# Revit family: 2061270 Sylvania Lighting Fixture DOMINO 10xLED 940 OPAL AY TRIM BLACK
name_source: partatom
category: Lighting Fixtures
revit_build: Autodesk Revit 2018 (Build: 20170223_1515(x64)
units: mm (PartAtom-declared; Revit-internal decimal feet)

## family parameters
Cut with Voids When Loaded = No
Host = Face
Light Source = Yes
OmniClass Number = 23.80.70.00
OmniClass Title = Lighting
Part Type = Normal
Room Calculation Point = No
Round Connector Dimension = Use Diameter
Shared = No

## types (1)
- 2061270 DOMINO 10XLED 940 OPAL ASYM TR BLK
    Apparent Load = 23 VA
    Assembly Code = D5020200
    AssetType = Fixed
    Body Length = 270 mm
    Body Width = 40 mm
    ClassificationName = Uniclass2015
    ClassificationValue = EF_70_80
    Color Filter = 16777215
    Cost = 0 $
    Default Elevation = 1219 mm
    Description = Modular LED recessed linear spotlight, ideal for retail and hospitality applications. Die-cast aluminium body, passive cooling. Two levels of reflector installation, low glaring. 10x LED source, asymmetric beam angle , optics: PMMA lens and polycarbonate reflector combination, opaline diffuser. Light color temperature: 4000K neutral white, total system power: 23W , total fixture lumen output: 1475lm, efficacy: 65 lm/W, Ra90 typical, LED chromacity: 3 step MacAdam ellipse (SDCM3), lifespan: 96,000 hours at 90% of the original output (L90B10), IR/UV free light source without heat radiation, operating voltage: 220-240V / 50-60Hz, electronic driver, ultra low flicker, non-dimmable , electrical protection: Class II. Degree of Protection: IP40/IP20, suitable for indoor environment only. Ceiling cut-out: 43x43mm, outer dimensions:  280x50mm trim frame RAL 9005 - Jet black color.5 years Warranty.
    Dimming Lamp Color Temperature Shift = <None>
    DocumentationLiterature = http://www.sylvania-lighting.com
    DurationUnit = hours
    ElectricShockClassification = 65
    Emit Shape Visible in Rendering = No
    Emit from Circle Diameter = 610 mm
    ExpectedLife = 50000
    Facia Height = 2 mm  [stored 0.00656168 ft]
    Facia internal length = 268 mm
    Facia internal width = 37 mm
    IfcExportAs = Class II
    IfcExportType = IfcLightFixtureType
    ImpactProtectionIndex = IfcLightFixtureType
    IngressProtection = IfcLightFixtureType
    InputNominalFrequency = 4000
    InputVoltage = 0
    LampColourRenderingIndex = 16500
    LampColourTemperature = LED
    LampMacAdamStep = 90
    LampNominalLuminous = 4000 K
    Length = 280 mm
    Lens = Glass, White, High Luminance
    Lens Outside recess = 32 mm
    Lens Width = 32 mm
    Lens inside recess = 25 mm  [stored 0.082021 ft]
    LightOutputRatio = LED
    LuminaireType = 0
    ManufacturerName = 65 lm/W
    Material = Feilo Sylvania
    Material_1_FEILO = <By Category>
    Material_2_FEILO = <By Category>
    Material_3_FEILO = <By Category>
    Material_4_FEILO = <By Category>
    Model = DOMINO 10xLED 940 OPAL AY TRIM BLACK
    ModelNumber = 2061270
    ModelReference = DOMINO 10xLED 940 OPAL AY TRIM BLACK
    Name = DOMINO 10xLED 940 OPAL AY TRIM BLACK
    NominalDepth = 0 mm  [stored 0 ft]
    NominalHeight = 0 mm  [stored 0 ft]
    NominalLength = 50 mm  [stored 0.164042 ft]
    Photometric Web File = 2061270.ies
    PowerConsumption = Lighting
    PowerFactor = 0
    Recessed Length = 276 mm  [stored 0.905512 ft]
    Recessed Width = 43 mm
    Tilt Angle = 90.00°
    Top Width = 26 mm
    Type Image = <None>
    TypeName = DOMINO 10xLED 940 OPAL AY TRIM BLACK
    URL = 0.95
    Voltage = 0 V
    WarrantyDescription = http://www.sylvania-lighting.com
    Width = 50 mm  [stored 0.164042 ft]
    top top length = 255 mm  [stored 0.836614 ft]
    top top width = 16 mm

note: [stored X ft] marks values corroborated as IEEE doubles in the binary element streams (Revit-internal decimal feet)

## geometry (parser evidence)
native form markers: Sweep x2
no freeform markers — native parametric forms only
